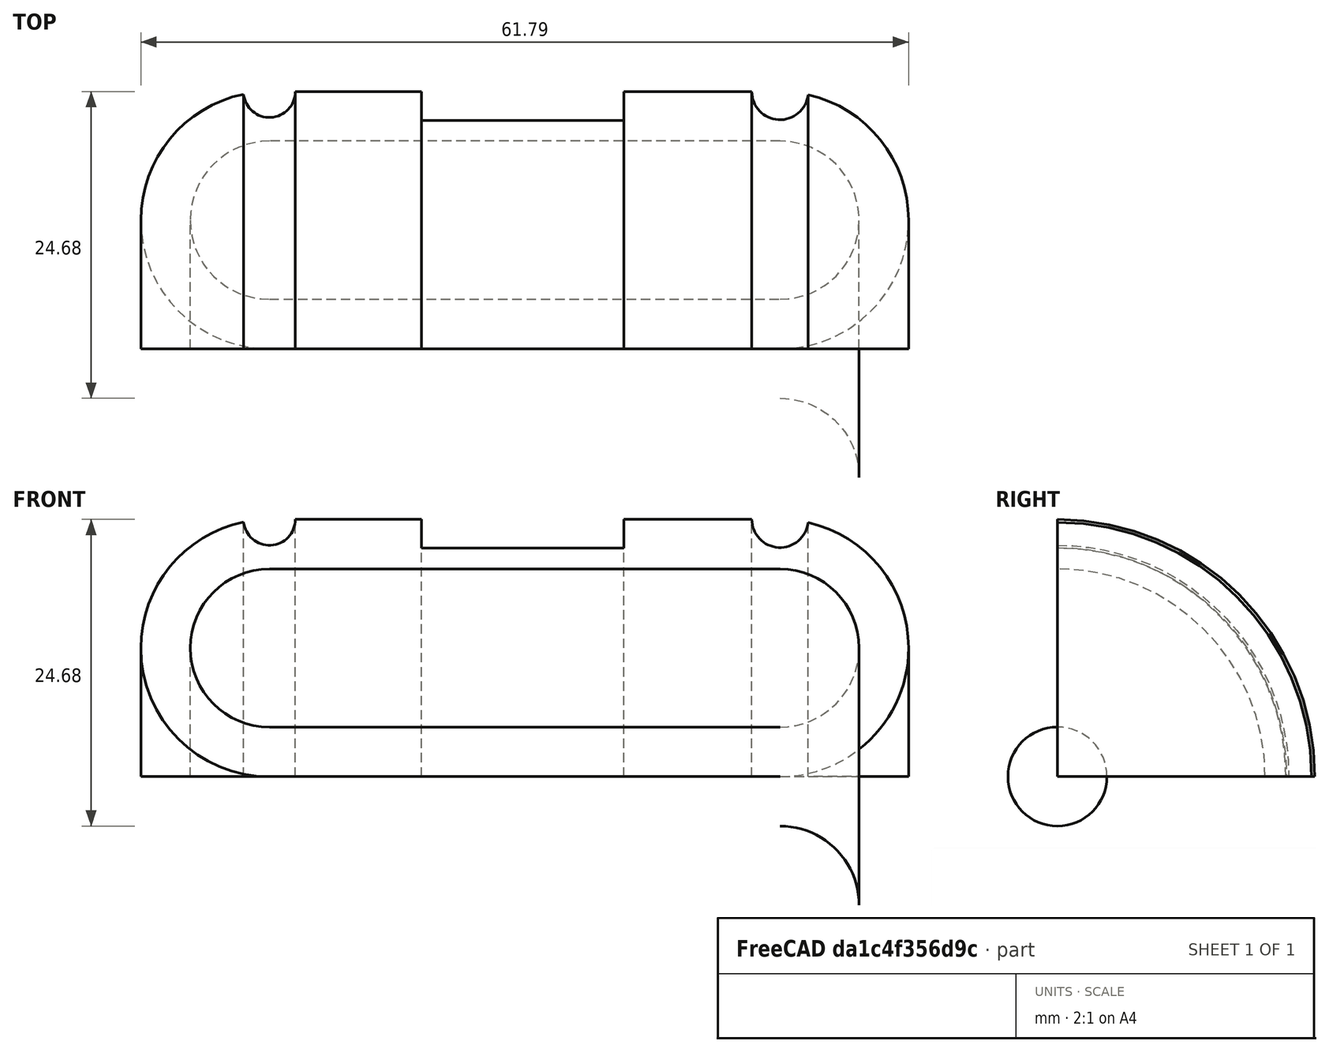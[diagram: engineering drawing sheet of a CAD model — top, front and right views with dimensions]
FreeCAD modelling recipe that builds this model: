
FCSTD DOCUMENT  (FreeCAD 0.20R29410 (Git))
Label: MangoJelly_Solutions_Tutorial_Ep8_4
License: All rights reserved
LicenseURL: http://en.wikipedia.org/wiki/All_rights_reserved
objects: Sketcher::SketchObject×2, Part::Extrusion×2, Part::Cut×1, Part::FeaturePython×1, Part::Revolution×1
note: 7 computed .brp shape members not serialized (recipe doc carries the construction recipe); baked Part::Feature solids carry a one-line shape summary decoded from their .brp

FEATURE [Sketcher::SketchObject] Sketch
  FullyConstrained = false
  sketch-geometry (8):
    g0: ArcOfCircle CenterX=-26.108 CenterY=14.599 CenterZ=0 NormalX=0 NormalY=0 NormalZ=1 AngleXU=0 Radius=6.36415 StartAngle=1.5708 EndAngle=4.71239
    g1: ArcOfCircle CenterX=14.9842 CenterY=14.599 CenterZ=0 NormalX=0 NormalY=0 NormalZ=1 AngleXU=0 Radius=6.36415 StartAngle=4.71239 EndAngle=7.85398
    g2: LineSegment StartX=-26.108 StartY=8.23489 StartZ=0 EndX=14.9842 EndY=8.23489 EndZ=0
    g3: LineSegment StartX=14.9842 StartY=20.9632 StartZ=0 EndX=-26.108 EndY=20.9632 EndZ=0
    g4: ArcOfCircle CenterX=-26.108 CenterY=14.599 CenterZ=0 NormalX=0 NormalY=0 NormalZ=1 AngleXU=0 Radius=10.3487 StartAngle=1.5708 EndAngle=4.71239
    g5: ArcOfCircle CenterX=14.9842 CenterY=14.599 CenterZ=0 NormalX=0 NormalY=0 NormalZ=1 AngleXU=0 Radius=10.3487 StartAngle=4.71239 EndAngle=7.85398
    g6: LineSegment StartX=-26.108 StartY=4.25029 StartZ=0 EndX=14.9842 EndY=4.25029 EndZ=0
    g7: LineSegment StartX=14.9842 StartY=24.9478 StartZ=0 EndX=-26.108 EndY=24.9478 EndZ=0
  constraints (13):
    c: Tangent(g0,g2) = -1.5708
    c: Tangent(g2,g1) = -1.5708
    c: Tangent(g1,g3) = -1.5708
    c: Tangent(g3,g0) = -1.5708
    c: Equal(g0,g1)
    c: Horizontal(g2)
    c: Tangent(g4,g6) = -1.5708
    c: Tangent(g6,g5) = -1.5708
    c: Tangent(g5,g7) = -1.5708
    c: Tangent(g7,g4) = -1.5708
    c: Equal(g4,g5)
    c: Coincident(g4,g0)
    c: Coincident(g5,g1)
FEATURE [Part::Extrusion] Extrude
  Base = -> Sketch
  Dir = (0,0,1)
  DirMode = 2
  FaceMakerClass = Part::FaceMakerBullseye
  LengthFwd = 15
  LengthRev = 0
  Solid = true
  Symmetric = false
FEATURE [Sketcher::SketchObject] Sketch001
  ExternalGeometry = -> [Extrude]
  FullyConstrained = false
  MapMode = 5
  Placement = pos=(0,0,15) rot=(0,0,1;0rad)
  Support = -> [Extrude]
  sketch-geometry (6):
    g0: Circle CenterX=-26.108 CenterY=24.9478 CenterZ=0 NormalX=0 NormalY=0 NormalZ=1 AngleXU=0 Radius=2.08108
    g1: Circle CenterX=14.9842 CenterY=24.9478 CenterZ=0 NormalX=0 NormalY=0 NormalZ=1 AngleXU=0 Radius=2.26591
    g2: LineSegment StartX=-13.8674 StartY=26.5105 StartZ=0 EndX=2.4189 EndY=26.5105 EndZ=0
    g3: LineSegment StartX=2.4189 StartY=26.5105 StartZ=0 EndX=2.4189 EndY=22.6375 EndZ=0
    g4: LineSegment StartX=2.4189 StartY=22.6375 StartZ=0 EndX=-13.8674 EndY=22.6375 EndZ=0
    g5: LineSegment StartX=-13.8674 StartY=22.6375 StartZ=0 EndX=-13.8674 EndY=26.5105 EndZ=0
  constraints (10):
    c: Coincident(g0,g-4)
    c: Coincident(g1,g-5)
    c: Coincident(g2,g3)
    c: Coincident(g3,g4)
    c: Coincident(g4,g5)
    c: Coincident(g5,g2)
    c: Horizontal(g2)
    c: Horizontal(g4)
    c: Vertical(g3)
    c: Vertical(g5)
FEATURE [Part::Extrusion] Extrude001
  Base = -> Sketch001
  Dir = (0,0,1)
  DirMode = 2
  FaceMakerClass = Part::FaceMakerBullseye
  LengthFwd = -7
  LengthRev = 0
  Solid = true
  Symmetric = false
FEATURE [Part::Cut] Cut
  Base = -> Extrude
  Tool = -> Extrude001
FEATURE [Part::FeaturePython] Facebinder  # WARN: FeaturePython — macro-defined, semantics opaque (R4)
  Area = 484.523
  Extrusion = 0
  Faces = -> [Cut]
  RemoveSplitter = false
  Sew = false
FEATURE [Part::Revolution] Revolve
  Angle = 90
  Axis = (1,0,0)
  Base = (-26.108,4.25029,15)
  FaceMakerClass = Part::FaceMakerBullseye
  Solid = false
  Source = -> Facebinder
  Symmetric = false
